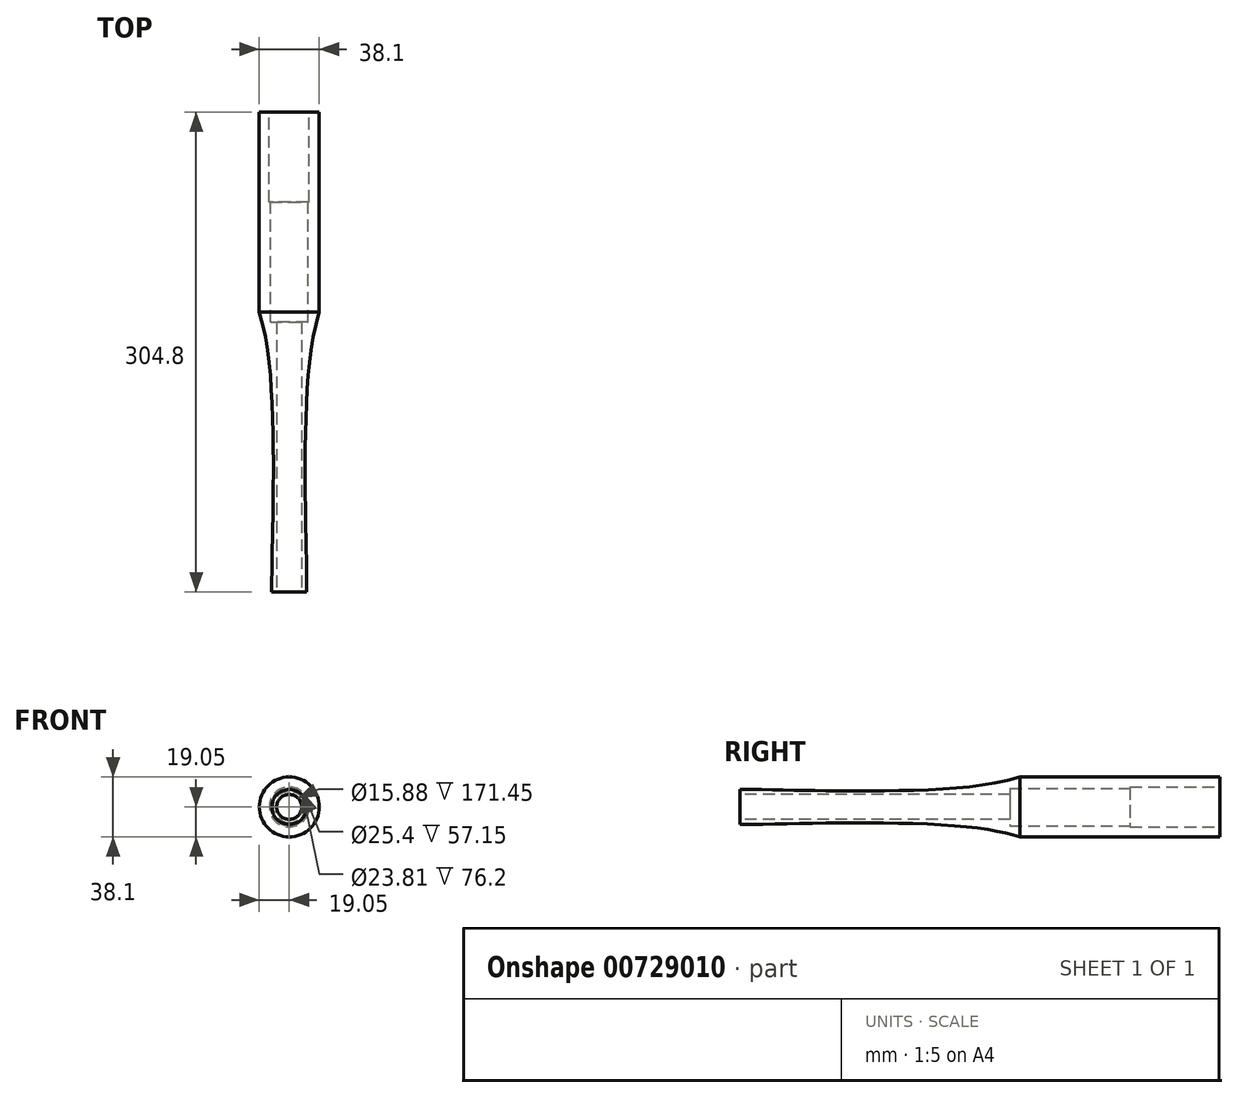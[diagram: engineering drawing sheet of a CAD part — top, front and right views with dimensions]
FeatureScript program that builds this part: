
annotation { "Feature Type Name" : "Feature", "Feature Type Description" : "" }
export const myFeature = defineFeature(function(context is Context, id is Id, definition is map)
    precondition{}
    {
        {
            var Q0;
            Q0=qCreatedBy(makeId("Right.planeOp"),FACE);
            var sketch = newSketch(context, id + "F0", { "sketchPlane" : qUnion([Q0])});
            skPoint(sketch, "E0", {"position": v(-304.8, 0) * mm});
            skFitSpline(sketch, "E1", {"points": [v(-304.8, 11.11) * mm, v(-241.3, 10.16) * mm, v(-160.02, 12.7) * mm, v(-127, 19.05) * mm], "startDerivative": vector(163.4, 0) * mm, "endDerivative": vector(98.8, 29.94) * mm});
            skLineSegment(sketch, "E2.bottom", {"start": v(-127, 19.05) * mm, "end": v(0, 19.05) * mm});
            skLineSegment(sketch, "E3", {"start": v(-304.8, 11.11) * mm, "end": v(-304.8, 0) * mm});
            skLineSegment(sketch, "E4", {"start": v(0, 19.05) * mm, "end": v(0, 0) * mm});
            skLineSegment(sketch, "E5", {"start": v(-304.8, 0) * mm, "end": v(0, 0) * mm});
            skSolve(sketch);
        }
        {
            var Q0;
            Q0 = qSketchRegion(id + "F0", true);
            var Q1;
            Q1=sQuery(id+"F0.wireOp",EDGE,"E5");
            revolve(context, id + "F1", {"surfaceOperationType" : NewSurfaceOperationType.NEW, "entities" : qUnion([Q0]), "axis" : qUnion([Q1]), "revolveType" : RevolveType.FULL});
        }
        {
            var Q0;
            Q0=makeQuery(id+"F1.opRevolve","SWEPT_FACE",FACE,{"disambiguationData":[OSD([sQuery(id+"F0.wireOp",EDGE,"E3")])]});
            var sketch = newSketch(context, id + "F2", { "sketchPlane" : qUnion([Q0])});
            skCircle(sketch, "E6", {"center": v(0, 0) * mm, "radius": 7.94 * mm});
            skSolve(sketch);
        }
        {
            var Q0;
            Q0 = qSketchRegion(id + "F2", true);
            extrude(context, id + "F3", {"entities" : qUnion([Q0]), "operationType" : NewBodyOperationType.REMOVE, "endBound" : BoundingType.THROUGH_ALL, "oppositeDirection" : true, "depth" : 25.4 * mm, "offsetDistance" : 25.4 * mm});
        }
        {
            var Q0;
            Q0=makeQuery(id+"F1.opRevolve","SWEPT_FACE",FACE,{"disambiguationData":[OSD([sQuery(id+"F0.wireOp",EDGE,"E4")])]});
            var sketch = newSketch(context, id + "F4", { "sketchPlane" : qUnion([Q0])});
            skCircle(sketch, "E7", {"center": v(0, 0) * mm, "radius": 12.7 * mm});
            skSolve(sketch);
        }
        {
            var Q0;
            Q0 = qSketchRegion(id + "F4", true);
            extrude(context, id + "F5", {"entities" : qUnion([Q0]), "operationType" : NewBodyOperationType.REMOVE, "oppositeDirection" : true, "depth" : 57.15 * mm, "offsetDistance" : 25.4 * mm});
        }
        {
            var Q0;
            Q0=makeQuery(id+"F5.boolean.opBoolean","COPY",FACE,{"derivedFrom":makeQuery(id+"F5.opExtrude","CAP_FACE",FACE,{"disambiguationData":[OSD([sQuery(id+"F4.wireOp",EDGE,"E7")])],"isStart":false})});
            var sketch = newSketch(context, id + "F6", { "sketchPlane" : qUnion([Q0])});
            skCircle(sketch, "E8", {"center": v(0, 0) * mm, "radius": 11.9 * mm});
            skSolve(sketch);
        }
        {
            var Q0;
            Q0 = qSketchRegion(id + "F6", true);
            extrude(context, id + "F7", {"entities" : qUnion([Q0]), "operationType" : NewBodyOperationType.REMOVE, "oppositeDirection" : true, "depth" : 76.2 * mm, "offsetDistance" : 25.4 * mm});
        }
    });
